# Revit family: AMEi6_RFA
name_source: partatom
category: Pipe Accessories
units: mm (PartAtom-declared; Revit-internal decimal feet)

## family parameters
Cut with Voids When Loaded = No
Host = Face
Part Type = Normal
Round Connector Dimension = Use Diameter
Shared = Yes

## types (4) — shared parameters
Control Input = 0-10V/0-20mA
Description = Actuator
Full Stroke Time = 30 min
H = 100 mm  [stored 0.328084 ft]
IfcExportType = IfcActuatorType
L = 220 mm  [stored 0.721785 ft]
Manufacturer = Danfoss
Max Medium Temperature = Depends on valve type. No limitations for 150 °C
Max Operating Torque = 7 Nm
Output Signal = 0-10V/0-20mA
Speed = 36 s/turn
URL = https://store.danfoss.com
W = 140 mm  [stored 0.459318 ft]
Weight = 2.50 kg
zero-valued in all types: Default Elevation

## per-type parameters (varying)
| type | IfcExportAs | Model | Model Type | Power Consumption | Power Supply |
| AMEi 6 iNET_24V_082G4303 | AMEi 6 iNET | 082G4303 | AMEi 6 iNET_24V | 8 VA | 24 V |
| AMEi 6 iNET_230V_082G4302 | AMEi 6 iNET | 082G4302 | AMEi 6 iNET_230V | 16 VA | 230 V |
| AMEi 6 iSET_24V_082G4301 | AMEi 6 iSET | 082G4301 | AMEi 6 iSET_24V | 8 VA | 24 V |
| AMEi 6 iSET_230V_082G4300 | AMEi 6 iSET | 082G4300 | AMEi 6 iSET_230V | 16 VA | 230 V |

note: [stored X ft] marks values corroborated as IEEE doubles in the binary element streams (Revit-internal decimal feet)

## geometry (parser evidence)
native form markers: Blend x2, Sweep x3
no freeform markers — native parametric forms only
